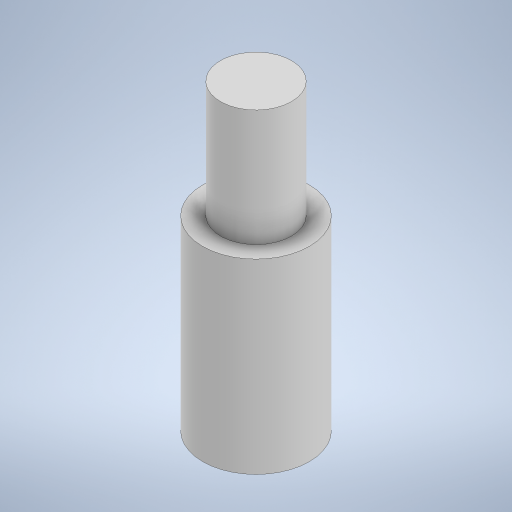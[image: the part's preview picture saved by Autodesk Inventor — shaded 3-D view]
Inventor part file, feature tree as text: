
AUTODESK INVENTOR PART (.ipt)
format: ipt  version: 2024 (Build 280153000, 153)  size: 231,936 bytes
history: native  units: in
note: dims shown in document units (in); Inventor stores cm internally (conversion verified against a paired STEP export)
features: extrude x2, sketch x2
ambient origin geometry x8: Origin, YZ Plane, XZ Plane, XY Plane, X Axis, Y Axis, Z Axis, Center Point
bodies: Solid1 (feature_tree)
feature tree (4):
  extrude  "Extrusion1"  Depth=0.315in TaperAngle=0.0deg
  extrude  "Extrusion3"  Depth=0.1969in TaperAngle=0.0deg
  sketch  "Sketch1"  dims[d0=0.18in d1=0.315in d2=0.0in]
  sketch  "Sketch3"  dims[d7=0.12in d8=0.1969in d9=0.0in]
